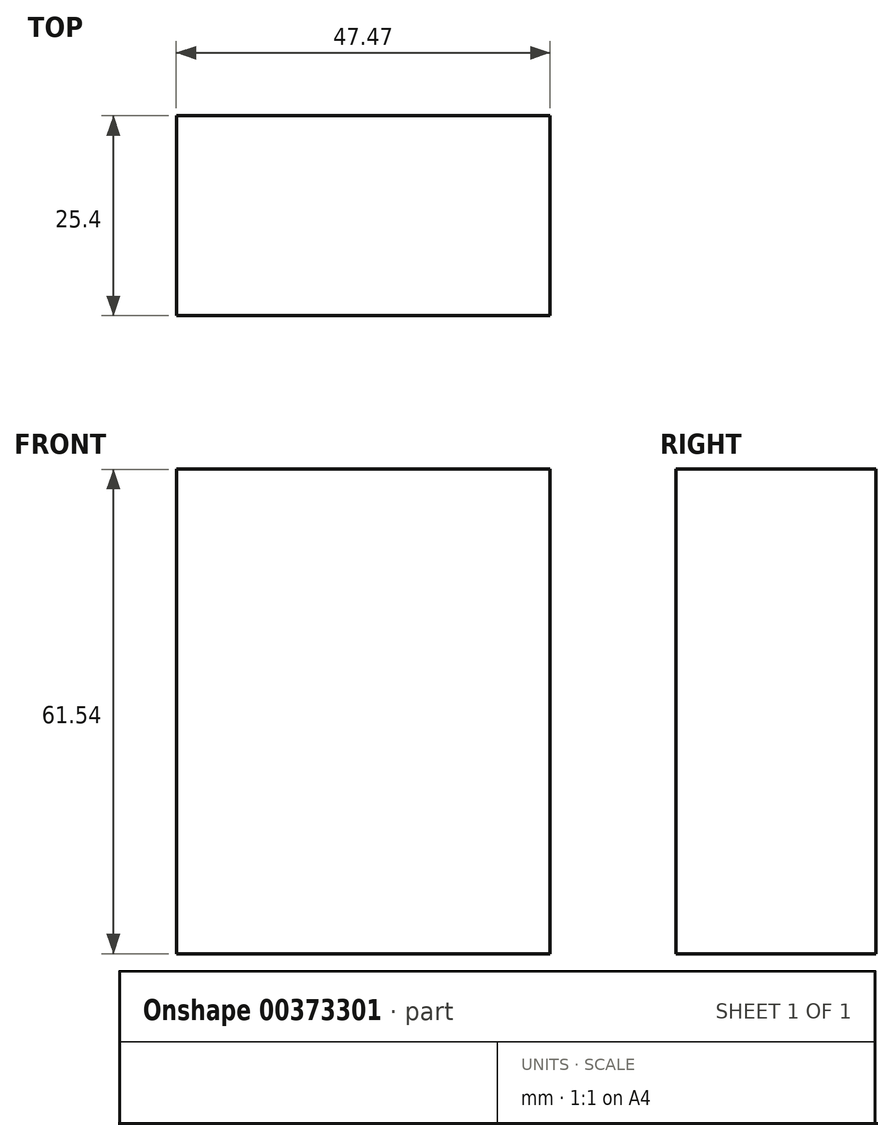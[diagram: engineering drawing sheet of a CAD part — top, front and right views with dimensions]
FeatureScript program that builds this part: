
annotation { "Feature Type Name" : "Feature", "Feature Type Description" : "" }
export const myFeature = defineFeature(function(context is Context, id is Id, definition is map)
    precondition{}
    {
        {
            var Q0;
            Q0=qCreatedBy(makeId("Front.planeOp"),FACE);
            var sketch = newSketch(context, id + "F0", { "sketchPlane" : qUnion([Q0])});
            skLineSegment(sketch, "E0.bottom", {"start": v(-63.36, 61.54) * mm, "end": v(-15.9, 61.54) * mm});
            skLineSegment(sketch, "E0.top", {"start": v(-63.36, 0) * mm, "end": v(-15.9, 0) * mm});
            skLineSegment(sketch, "E0.left", {"start": v(-63.36, 61.54) * mm, "end": v(-63.36, 0) * mm});
            skLineSegment(sketch, "E0.right", {"start": v(-15.9, 61.54) * mm, "end": v(-15.9, 0) * mm});
            skSolve(sketch);
        }
        {
            var Q0;
            Q0 = qSketchRegion(id + "F0", true);
            extrude(context, id + "F1", {"entities" : qUnion([Q0]), "depth" : 25.4 * mm});
        }
    });
